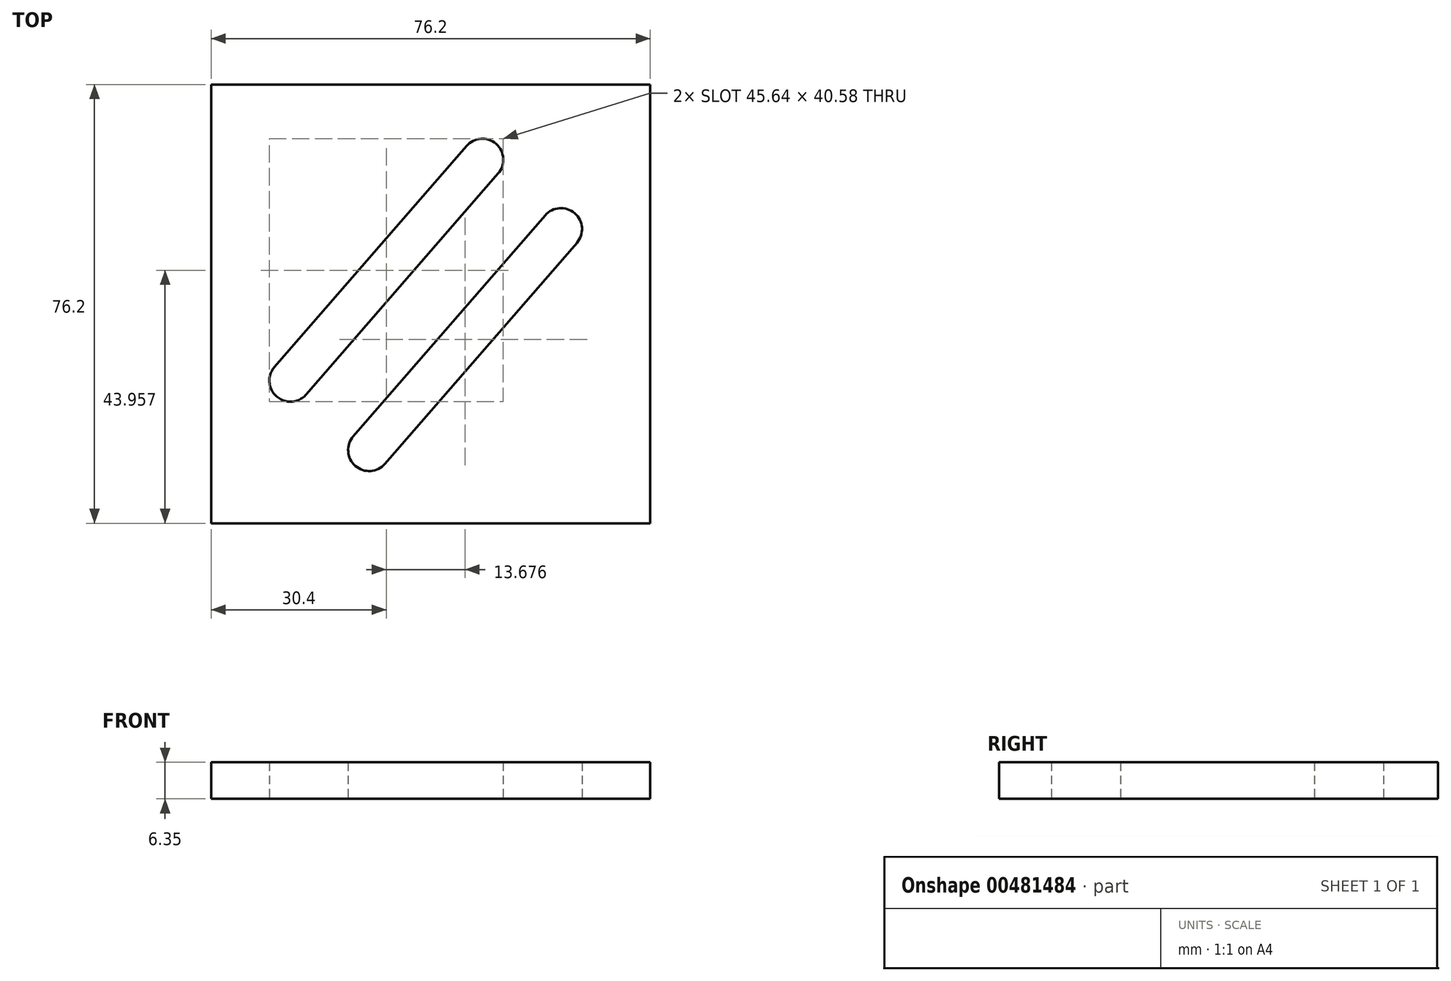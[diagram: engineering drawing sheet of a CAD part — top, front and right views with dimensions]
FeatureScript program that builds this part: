
annotation { "Feature Type Name" : "Feature", "Feature Type Description" : "" }
export const myFeature = defineFeature(function(context is Context, id is Id, definition is map)
    precondition{}
    {
        {
            var Q0;
            Q0=qCreatedBy(makeId("Top.planeOp"),FACE);
            var sketch = newSketch(context, id + "F0", { "sketchPlane" : qUnion([Q0])});
            skLineSegment(sketch, "E0.bottom", {"start": v(-38.1, 38.1) * mm, "end": v(38.1, 38.1) * mm});
            skLineSegment(sketch, "E0.top", {"start": v(-38.1, -38.1) * mm, "end": v(38.1, -38.1) * mm});
            skLineSegment(sketch, "E0.left", {"start": v(-38.1, 38.1) * mm, "end": v(-38.1, -38.1) * mm});
            skLineSegment(sketch, "E0.right", {"start": v(38.1, 38.1) * mm, "end": v(38.1, -38.1) * mm});
            skPoint(sketch, "E0.middle", {"position": v(0, 0) * mm});
            skLineSegment(sketch, "E1", {"start": v(-27.1, -10.93) * mm, "end": v(6.2, 27.43) * mm});
            skLineSegment(sketch, "E2", {"start": v(-21.6, -15.71) * mm, "end": v(11.7, 22.65) * mm});
            skArc(sketch, "E3", {"start": v(-27.1, -10.93) * mm, "mid": v(-26.74, -16.08) * mm, "end": v(-21.6, -15.71) * mm});
            skArc(sketch, "E4", {"start": v(11.7, 22.65) * mm, "mid": v(11.34, 27.8) * mm, "end": v(6.2, 27.43) * mm});
            skPoint(sketch, "E5.middle", {"position": v(13.68, -12.05) * mm});
            skLineSegment(sketch, "E6", {"start": v(-13.43, -22.98) * mm, "end": v(19.87, 15.38) * mm});
            skLineSegment(sketch, "E7", {"start": v(-7.92, -27.77) * mm, "end": v(25.38, 10.6) * mm});
            skArc(sketch, "E8", {"start": v(-13.43, -22.98) * mm, "mid": v(-13.07, -28.13) * mm, "end": v(-7.92, -27.77) * mm});
            skArc(sketch, "E9", {"start": v(25.38, 10.6) * mm, "mid": v(25.02, 15.74) * mm, "end": v(19.87, 15.38) * mm});
            skSolve(sketch);
        }
        {
            var Q0;
            Q0=makeQuery(id+"F0.imprint","IMPRINT",FACE,{"disambiguationData":[TD([[makeQuery(id+"F0.imprint","IMPRINT",EDGE,{"derivedFrom":sQuery(id+"F0.wireOp",EDGE,"E0.bottom")}),-1.0]])]});
            extrude(context, id + "F1", {"entities" : qUnion([Q0]), "depth" : 6.35 * mm});
        }
    });
